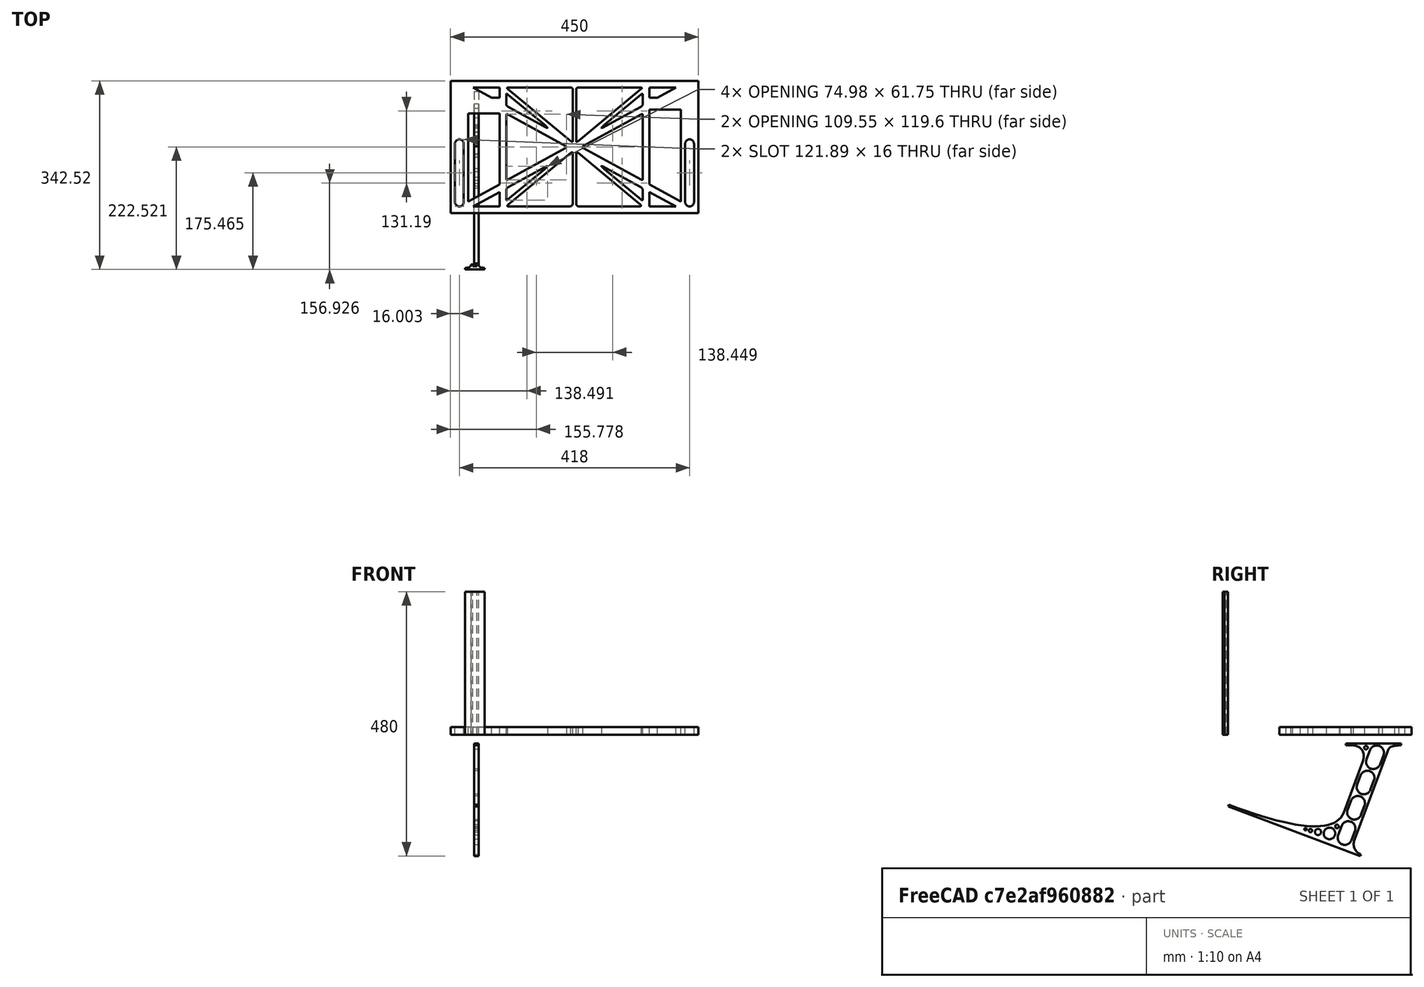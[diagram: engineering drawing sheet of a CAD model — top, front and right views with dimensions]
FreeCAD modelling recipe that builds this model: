
FCSTD DOCUMENT  (FreeCAD 0.19R0.19.2)
Label: laptopStand091
License: All rights reserved
LicenseURL: http://en.wikipedia.org/wiki/All_rights_reserved
objects: Sketcher::SketchObject×3, Part::Extrusion×3
note: 6 computed .brp shape members not serialized (recipe doc carries the construction recipe); baked Part::Feature solids carry a one-line shape summary decoded from their .brp

FEATURE [Sketcher::SketchObject] Sketch
  FullyConstrained = true
  sketch-geometry (244):
    g0: LineSegment StartX=-10.9272 StartY=-82.7794 StartZ=0 EndX=46.0728 EndY=-51.4823 EndZ=0
    g1: LineSegment StartX=366.073 StartY=-91.7794 StartZ=0 EndX=318.073 EndY=-65.424 EndZ=0
    g2: LineSegment StartX=-10.9272 StartY=77.3346 StartZ=0 EndX=-10.9272 EndY=-82.7794 EndZ=0
    g3: LineSegment StartX=375.073 StartY=-82.7794 StartZ=0 EndX=375.073 EndY=83.9235 EndZ=0
    g4: LineSegment StartX=-1.92719 StartY=-91.7794 StartZ=0 EndX=46.0728 EndY=-91.7794 EndZ=0
    g5: LineSegment StartX=318.073 StartY=124.221 StartZ=0 EndX=366.073 EndY=124.221 EndZ=0
    g6: LineSegment StartX=318.073 StartY=83.9235 StartZ=0 EndX=318.073 EndY=-51.4823 EndZ=0
    g7: LineSegment StartX=318.073 StartY=-51.4823 StartZ=0 EndX=375.073 EndY=-82.7794 EndZ=0
    g8: LineSegment StartX=318.073 StartY=-65.424 StartZ=0 EndX=318.073 EndY=-91.7794 EndZ=0
    g9: LineSegment StartX=318.073 StartY=-91.7794 StartZ=0 EndX=366.073 EndY=-91.7794 EndZ=0
    g10: LineSegment StartX=46.0728 StartY=-65.424 StartZ=0 EndX=-1.92719 EndY=-91.7794 EndZ=0
    g11: LineSegment StartX=46.0728 StartY=-65.424 StartZ=0 EndX=46.0728 EndY=-91.7794 EndZ=0
    g12: LineSegment StartX=46.0728 StartY=77.3346 StartZ=0 EndX=46.0728 EndY=-51.4823 EndZ=0
    g13: LineSegment StartX=-42.9272 StartY=136.221 StartZ=0 EndX=-42.9272 EndY=-103.779 EndZ=0
    g14: LineSegment StartX=407.073 StartY=136.221 StartZ=0 EndX=407.073 EndY=-103.779 EndZ=0
    g15: ArcOfCircle CenterX=-26.9272 CenterY=22.1087 CenterZ=0 NormalX=0 NormalY=0 NormalZ=1 AngleXU=0 Radius=8 StartAngle=1e-16 EndAngle=3.14159
    g16: ArcOfCircle CenterX=-26.9272 CenterY=-83.7794 CenterZ=0 NormalX=0 NormalY=0 NormalZ=1 AngleXU=0 Radius=8 StartAngle=3.14159 EndAngle=6.28319
    g17: LineSegment StartX=-34.9272 StartY=22.1087 StartZ=0 EndX=-34.9272 EndY=-83.7794 EndZ=0
    g18: LineSegment StartX=-18.9272 StartY=22.1087 StartZ=0 EndX=-18.9272 EndY=-83.7794 EndZ=0
    g19: ArcOfCircle CenterX=391.073 CenterY=22.1087 CenterZ=0 NormalX=0 NormalY=0 NormalZ=1 AngleXU=0 Radius=8 StartAngle=-4.4e-15 EndAngle=3.14159
    g20: LineSegment StartX=399.073 StartY=22.1087 StartZ=0 EndX=399.073 EndY=-83.7794 EndZ=0
    g21: LineSegment StartX=383.073 StartY=22.1087 StartZ=0 EndX=383.073 EndY=-83.7794 EndZ=0
    g22: ArcOfCircle CenterX=391.073 CenterY=-83.7794 CenterZ=0 NormalX=0 NormalY=0 NormalZ=1 AngleXU=0 Radius=8 StartAngle=3.14159 EndAngle=6.28319
    g23: Circle CenterX=175.022 CenterY=27.0628 CenterZ=0 NormalX=0 NormalY=0 NormalZ=1 AngleXU=0 Radius=1
    g24: Circle CenterX=179.022 CenterY=24.8665 CenterZ=0 NormalX=0 NormalY=0 NormalZ=1 AngleXU=0 Radius=1
    g25: Circle CenterX=179.022 CenterY=27.0628 CenterZ=0 NormalX=0 NormalY=0 NormalZ=1 AngleXU=0 Radius=1
    g26: BSplineCurve PolesCount=3 KnotsCount=2 Degree=2 IsPeriodic=0
    g27: GeomPoint X=175.022 Y=27.0628 Z=0
    g28: GeomPoint X=179.022 Y=27.0628 Z=0
    g29: Circle CenterX=189.124 CenterY=27.0628 CenterZ=0 NormalX=0 NormalY=0 NormalZ=1 AngleXU=0 Radius=1
    g30: Circle CenterX=185.124 CenterY=24.8665 CenterZ=0 NormalX=0 NormalY=0 NormalZ=1 AngleXU=0 Radius=1
    g31: Circle CenterX=185.124 CenterY=27.0628 CenterZ=0 NormalX=0 NormalY=0 NormalZ=1 AngleXU=0 Radius=1
    g32: BSplineCurve PolesCount=3 KnotsCount=2 Degree=2 IsPeriodic=0
    g33: GeomPoint X=189.124 Y=27.0628 Z=0
    g34: GeomPoint X=185.124 Y=27.0628 Z=0
    g35: Circle CenterX=175.022 CenterY=5.37834 CenterZ=0 NormalX=0 NormalY=0 NormalZ=1 AngleXU=0 Radius=1
    g36: Circle CenterX=179.022 CenterY=7.57463 CenterZ=0 NormalX=0 NormalY=0 NormalZ=1 AngleXU=0 Radius=1
    g37: Circle CenterX=179.022 CenterY=5.34704 CenterZ=0 NormalX=0 NormalY=0 NormalZ=1 AngleXU=0 Radius=1
    g38: BSplineCurve PolesCount=3 KnotsCount=2 Degree=2 IsPeriodic=0
    g39: GeomPoint X=175.022 Y=5.37834 Z=0
    g40: GeomPoint X=179.022 Y=5.34704 Z=0
    g41: Circle CenterX=189.124 CenterY=5.37834 CenterZ=0 NormalX=0 NormalY=0 NormalZ=1 AngleXU=0 Radius=1
    g42: Circle CenterX=185.124 CenterY=7.57463 CenterZ=0 NormalX=0 NormalY=0 NormalZ=1 AngleXU=0 Radius=1
    g43: Circle CenterX=185.124 CenterY=5.34704 CenterZ=0 NormalX=0 NormalY=0 NormalZ=1 AngleXU=0 Radius=1
    g44: BSplineCurve PolesCount=3 KnotsCount=2 Degree=2 IsPeriodic=0
    g45: GeomPoint X=189.124 Y=5.37834 Z=0
    g46: GeomPoint X=185.124 Y=5.34704 Z=0
    g47: Circle CenterX=165.871 CenterY=18.1458 CenterZ=0 NormalX=0 NormalY=0 NormalZ=1 AngleXU=0 Radius=1
    g48: Circle CenterX=169.377 CenterY=16.2206 CenterZ=0 NormalX=0 NormalY=0 NormalZ=1 AngleXU=0 Radius=1
    g49: Circle CenterX=165.871 CenterY=14.2954 CenterZ=0 NormalX=0 NormalY=0 NormalZ=1 AngleXU=0 Radius=1
    g50: BSplineCurve PolesCount=3 KnotsCount=2 Degree=2 IsPeriodic=0
    g51: GeomPoint X=165.871 Y=18.1458 Z=0
    g52: GeomPoint X=165.871 Y=14.2954 Z=0
    g53: Circle CenterX=198.275 CenterY=18.1458 CenterZ=0 NormalX=0 NormalY=0 NormalZ=1 AngleXU=0 Radius=1
    g54: Circle CenterX=194.768 CenterY=16.2206 CenterZ=0 NormalX=0 NormalY=0 NormalZ=1 AngleXU=0 Radius=1
    g55: Circle CenterX=198.275 CenterY=14.2954 CenterZ=0 NormalX=0 NormalY=0 NormalZ=1 AngleXU=0 Radius=1
    g56: BSplineCurve PolesCount=3 KnotsCount=2 Degree=2 IsPeriodic=0
    g57: GeomPoint X=198.275 Y=18.1458 Z=0
    g58: GeomPoint X=198.275 Y=14.2954 Z=0
    g59: LineSegment StartX=407.073 StartY=-103.779 StartZ=0 EndX=-42.9272 EndY=-103.779 EndZ=0
    g60: LineSegment StartX=407.073 StartY=136.221 StartZ=0 EndX=-42.9272 EndY=136.221 EndZ=0
    g61: LineSegment StartX=46.0728 StartY=77.3346 StartZ=0 EndX=-10.9272 EndY=77.3346 EndZ=0
    g62: LineSegment StartX=46.0728 StartY=105.865 StartZ=0 EndX=31.5028 EndY=105.865 EndZ=0
    g63: LineSegment StartX=46.0728 StartY=124.221 StartZ=0 EndX=46.0728 EndY=105.865 EndZ=0
    g64: LineSegment StartX=-1.92719 StartY=124.221 StartZ=0 EndX=31.5028 EndY=105.865 EndZ=0
    g65: LineSegment StartX=46.0728 StartY=124.221 StartZ=0 EndX=-1.92719 EndY=124.221 EndZ=0
    g66: LineSegment StartX=318.073 StartY=83.9235 StartZ=0 EndX=375.073 EndY=83.9235 EndZ=0
    g67: LineSegment StartX=318.073 StartY=105.865 StartZ=0 EndX=332.643 EndY=105.865 EndZ=0
    g68: LineSegment StartX=332.643 StartY=105.865 StartZ=0 EndX=366.073 EndY=124.221 EndZ=0
    g69: LineSegment StartX=318.073 StartY=124.221 StartZ=0 EndX=318.073 EndY=105.865 EndZ=0
    g70: Circle CenterX=125.607 CenterY=54.1951 CenterZ=0 NormalX=0 NormalY=0 NormalZ=1 AngleXU=0 Radius=1
    g71: Circle CenterX=139.632 CenterY=46.4944 CenterZ=0 NormalX=0 NormalY=0 NormalZ=1 AngleXU=0 Radius=1
    g72: Circle CenterX=127.326 CenterY=56.7187 CenterZ=0 NormalX=0 NormalY=0 NormalZ=1 AngleXU=0 Radius=1
    g73: BSplineCurve PolesCount=3 KnotsCount=2 Degree=2 IsPeriodic=0
    g74: GeomPoint X=125.607 Y=54.1951 Z=0
    g75: GeomPoint X=127.326 Y=56.7187 Z=0
    g76: Circle CenterX=236.821 CenterY=56.7187 CenterZ=0 NormalX=0 NormalY=0 NormalZ=1 AngleXU=0 Radius=1
    g77: Circle CenterX=224.513 CenterY=46.4944 CenterZ=0 NormalX=0 NormalY=0 NormalZ=1 AngleXU=0 Radius=1
    g78: Circle CenterX=238.538 CenterY=54.1951 CenterZ=0 NormalX=0 NormalY=0 NormalZ=1 AngleXU=0 Radius=1
    g79: BSplineCurve PolesCount=3 KnotsCount=2 Degree=2 IsPeriodic=0
    g80: GeomPoint X=236.821 Y=56.7187 Z=0
    g81: GeomPoint X=238.538 Y=54.1951 Z=0
    g82: Circle CenterX=238.538 CenterY=-21.7539 CenterZ=0 NormalX=0 NormalY=0 NormalZ=1 AngleXU=0 Radius=1
    g83: Circle CenterX=224.513 CenterY=-14.0532 CenterZ=0 NormalX=0 NormalY=0 NormalZ=1 AngleXU=0 Radius=1
    g84: Circle CenterX=236.821 CenterY=-24.2775 CenterZ=0 NormalX=0 NormalY=0 NormalZ=1 AngleXU=0 Radius=1
    g85: BSplineCurve PolesCount=3 KnotsCount=2 Degree=2 IsPeriodic=0
    g86: GeomPoint X=238.538 Y=-21.7539 Z=0
    g87: GeomPoint X=236.821 Y=-24.2775 Z=0
    g88: Circle CenterX=125.607 CenterY=-21.7539 CenterZ=0 NormalX=0 NormalY=0 NormalZ=1 AngleXU=0 Radius=1
    g89: Circle CenterX=139.632 CenterY=-14.0532 CenterZ=0 NormalX=0 NormalY=0 NormalZ=1 AngleXU=0 Radius=1
    g90: Circle CenterX=127.325 CenterY=-24.2775 CenterZ=0 NormalX=0 NormalY=0 NormalZ=1 AngleXU=0 Radius=1
    g91: BSplineCurve PolesCount=3 KnotsCount=2 Degree=2 IsPeriodic=0
    g92: GeomPoint X=125.607 Y=-21.7539 Z=0
    g93: GeomPoint X=127.325 Y=-24.2775 Z=0
    g94: Circle CenterX=302.996 CenterY=111.695 CenterZ=0 NormalX=0 NormalY=0 NormalZ=1 AngleXU=0 Radius=1
    g95: Circle CenterX=306.073 CenterY=114.251 CenterZ=0 NormalX=0 NormalY=0 NormalZ=1 AngleXU=0 Radius=1
    g96: Circle CenterX=306.073 CenterY=110.251 CenterZ=0 NormalX=0 NormalY=0 NormalZ=1 AngleXU=0 Radius=1
    g97: BSplineCurve PolesCount=3 KnotsCount=2 Degree=2 IsPeriodic=0
    g98: GeomPoint X=302.996 Y=111.695 Z=0
    g99: GeomPoint X=306.073 Y=110.251 Z=0
    g100: Circle CenterX=306.073 CenterY=95.2763 CenterZ=0 NormalX=0 NormalY=0 NormalZ=1 AngleXU=0 Radius=1
    g101: Circle CenterX=306.073 CenterY=91.2763 CenterZ=0 NormalX=0 NormalY=0 NormalZ=1 AngleXU=0 Radius=1
    g102: Circle CenterX=302.567 CenterY=89.3511 CenterZ=0 NormalX=0 NormalY=0 NormalZ=1 AngleXU=0 Radius=1
    g103: BSplineCurve PolesCount=3 KnotsCount=2 Degree=2 IsPeriodic=0
    g104: GeomPoint X=306.073 Y=95.2763 Z=0
    g105: GeomPoint X=302.567 Y=89.3511 Z=0
    g106: LineSegment StartX=306.073 StartY=110.251 StartZ=0 EndX=306.073 EndY=95.2763 EndZ=0
    g107: LineSegment StartX=302.996 StartY=111.695 StartZ=0 EndX=236.821 EndY=56.7187 EndZ=0
    g108: LineSegment StartX=238.538 StartY=54.1951 StartZ=0 EndX=302.567 EndY=89.3511 EndZ=0
    g109: Circle CenterX=61.1496 CenterY=111.695 CenterZ=0 NormalX=0 NormalY=0 NormalZ=1 AngleXU=0 Radius=1
    g110: Circle CenterX=58.0728 CenterY=114.251 CenterZ=0 NormalX=0 NormalY=0 NormalZ=1 AngleXU=0 Radius=1
    g111: Circle CenterX=58.0728 CenterY=110.251 CenterZ=0 NormalX=0 NormalY=0 NormalZ=1 AngleXU=0 Radius=1
    g112: BSplineCurve PolesCount=3 KnotsCount=2 Degree=2 IsPeriodic=0
    g113: GeomPoint X=61.1496 Y=111.695 Z=0
    g114: GeomPoint X=58.0728 Y=110.251 Z=0
    g115: Circle CenterX=61.5791 CenterY=89.3511 CenterZ=0 NormalX=0 NormalY=0 NormalZ=1 AngleXU=0 Radius=1
    g116: Circle CenterX=58.0728 CenterY=91.2763 CenterZ=0 NormalX=0 NormalY=0 NormalZ=1 AngleXU=0 Radius=1
    g117: Circle CenterX=58.0728 CenterY=95.2763 CenterZ=0 NormalX=0 NormalY=0 NormalZ=1 AngleXU=0 Radius=1
    g118: BSplineCurve PolesCount=3 KnotsCount=2 Degree=2 IsPeriodic=0
    g119: GeomPoint X=61.5791 Y=89.3511 Z=0
    g120: GeomPoint X=58.0728 Y=95.2763 Z=0
    g121: LineSegment StartX=58.0728 StartY=110.251 StartZ=0 EndX=58.0728 EndY=95.2763 EndZ=0
    g122: LineSegment StartX=61.1496 StartY=111.695 StartZ=0 EndX=127.326 EndY=56.7187 EndZ=0
    g123: LineSegment StartX=125.607 StartY=54.1951 StartZ=0 EndX=61.5791 EndY=89.3511 EndZ=0
    g124: Circle CenterX=61.5791 CenterY=-56.9099 CenterZ=0 NormalX=0 NormalY=0 NormalZ=1 AngleXU=0 Radius=1
    g125: Circle CenterX=58.0728 CenterY=-58.8351 CenterZ=0 NormalX=0 NormalY=0 NormalZ=1 AngleXU=0 Radius=1
    g126: Circle CenterX=58.0728 CenterY=-62.8351 CenterZ=0 NormalX=0 NormalY=0 NormalZ=1 AngleXU=0 Radius=1
    g127: BSplineCurve PolesCount=3 KnotsCount=2 Degree=2 IsPeriodic=0
    g128: GeomPoint X=61.5791 Y=-56.9099 Z=0
    g129: GeomPoint X=58.0728 Y=-62.8351 Z=0
    g130: Circle CenterX=58.0728 CenterY=-77.8102 CenterZ=0 NormalX=0 NormalY=0 NormalZ=1 AngleXU=0 Radius=1
    g131: Circle CenterX=58.0728 CenterY=-81.8102 CenterZ=0 NormalX=0 NormalY=0 NormalZ=1 AngleXU=0 Radius=1
    g132: Circle CenterX=61.1496 CenterY=-79.2541 CenterZ=0 NormalX=0 NormalY=0 NormalZ=1 AngleXU=0 Radius=1
    g133: BSplineCurve PolesCount=3 KnotsCount=2 Degree=2 IsPeriodic=0
    g134: GeomPoint X=58.0728 Y=-77.8102 Z=0
    g135: GeomPoint X=61.1496 Y=-79.2541 Z=0
    g136: LineSegment StartX=58.0728 StartY=-62.8351 StartZ=0 EndX=58.0728 EndY=-77.8102 EndZ=0
    g137: LineSegment StartX=61.1496 StartY=-79.2541 StartZ=0 EndX=127.325 EndY=-24.2775 EndZ=0
    g138: LineSegment StartX=125.607 StartY=-21.7539 StartZ=0 EndX=61.5791 EndY=-56.9099 EndZ=0
    g139: Circle CenterX=302.567 CenterY=-56.9099 CenterZ=0 NormalX=0 NormalY=0 NormalZ=1 AngleXU=0 Radius=1
    g140: Circle CenterX=306.073 CenterY=-58.8351 CenterZ=0 NormalX=0 NormalY=0 NormalZ=1 AngleXU=0 Radius=1
    g141: Circle CenterX=306.073 CenterY=-62.8351 CenterZ=0 NormalX=0 NormalY=0 NormalZ=1 AngleXU=0 Radius=1
    g142: BSplineCurve PolesCount=3 KnotsCount=2 Degree=2 IsPeriodic=0
    g143: GeomPoint X=302.567 Y=-56.9099 Z=0
    g144: GeomPoint X=306.073 Y=-62.8351 Z=0
    g145: Circle CenterX=302.996 CenterY=-79.2541 CenterZ=0 NormalX=0 NormalY=0 NormalZ=1 AngleXU=0 Radius=1
    g146: Circle CenterX=306.073 CenterY=-81.8102 CenterZ=0 NormalX=0 NormalY=0 NormalZ=1 AngleXU=0 Radius=1
    g147: Circle CenterX=306.073 CenterY=-77.8102 CenterZ=0 NormalX=0 NormalY=0 NormalZ=1 AngleXU=0 Radius=1
    g148: BSplineCurve PolesCount=3 KnotsCount=2 Degree=2 IsPeriodic=0
    g149: GeomPoint X=302.996 Y=-79.2541 Z=0
    g150: GeomPoint X=306.073 Y=-77.8102 Z=0
    g151: LineSegment StartX=306.073 StartY=-62.8351 StartZ=0 EndX=306.073 EndY=-77.8102 EndZ=0
    g152: LineSegment StartX=302.996 StartY=-79.2541 StartZ=0 EndX=236.821 EndY=-24.2775 EndZ=0
    g153: LineSegment StartX=238.538 StartY=-21.7539 StartZ=0 EndX=302.567 EndY=-56.9099 EndZ=0
    g154: Circle CenterX=61.6457 CenterY=-88.8112 CenterZ=0 NormalX=0 NormalY=0 NormalZ=1 AngleXU=0 Radius=1
    g155: Circle CenterX=58.0728 CenterY=-91.7794 CenterZ=0 NormalX=0 NormalY=0 NormalZ=1 AngleXU=0 Radius=1
    g156: Circle CenterX=63.9135 CenterY=-91.7794 CenterZ=0 NormalX=0 NormalY=0 NormalZ=1 AngleXU=0 Radius=1
    g157: BSplineCurve PolesCount=3 KnotsCount=2 Degree=2 IsPeriodic=0
    g158: GeomPoint X=61.6457 Y=-88.8112 Z=0
    g159: GeomPoint X=63.9135 Y=-91.7794 Z=0
    g160: Circle CenterX=179.022 CenterY=-85.8163 CenterZ=0 NormalX=0 NormalY=0 NormalZ=1 AngleXU=0 Radius=1
    g161: Circle CenterX=179.022 CenterY=-91.7794 CenterZ=0 NormalX=0 NormalY=0 NormalZ=1 AngleXU=0 Radius=1
    g162: Circle CenterX=171.895 CenterY=-91.7794 CenterZ=0 NormalX=0 NormalY=0 NormalZ=1 AngleXU=0 Radius=1
    g163: BSplineCurve PolesCount=3 KnotsCount=2 Degree=2 IsPeriodic=0
    g164: GeomPoint X=179.022 Y=-85.8163 Z=0
    g165: GeomPoint X=171.895 Y=-91.7794 Z=0
    g166: Circle CenterX=185.124 CenterY=-86.2028 CenterZ=0 NormalX=0 NormalY=0 NormalZ=1 AngleXU=0 Radius=1
    g167: Circle CenterX=185.124 CenterY=-91.7794 CenterZ=0 NormalX=0 NormalY=0 NormalZ=1 AngleXU=0 Radius=1
    g168: Circle CenterX=191.747 CenterY=-91.7794 CenterZ=0 NormalX=0 NormalY=0 NormalZ=1 AngleXU=0 Radius=1
    g169: BSplineCurve PolesCount=3 KnotsCount=2 Degree=2 IsPeriodic=0
    g170: GeomPoint X=185.124 Y=-86.2028 Z=0
    g171: GeomPoint X=191.747 Y=-91.7794 Z=0
    g172: Circle CenterX=299.888 CenterY=-86.6413 CenterZ=0 NormalX=0 NormalY=0 NormalZ=1 AngleXU=0 Radius=1
    g173: Circle CenterX=306.073 CenterY=-91.7794 CenterZ=0 NormalX=0 NormalY=0 NormalZ=1 AngleXU=0 Radius=1
    g174: Circle CenterX=298.776 CenterY=-91.7794 CenterZ=0 NormalX=0 NormalY=0 NormalZ=1 AngleXU=0 Radius=1
    g175: BSplineCurve PolesCount=3 KnotsCount=2 Degree=2 IsPeriodic=0
    g176: GeomPoint X=299.888 Y=-86.6413 Z=0
    g177: GeomPoint X=298.776 Y=-91.7794 Z=0
    g178: LineSegment StartX=189.124 StartY=5.37834 StartZ=0 EndX=299.888 EndY=-86.6413 EndZ=0
    g179: LineSegment StartX=298.776 StartY=-91.7794 StartZ=0 EndX=191.747 EndY=-91.7794 EndZ=0
    g180: LineSegment StartX=185.124 StartY=-86.2028 StartZ=0 EndX=185.124 EndY=5.34704 EndZ=0
    g181: LineSegment StartX=179.022 StartY=5.34704 StartZ=0 EndX=179.022 EndY=-85.8163 EndZ=0
    g182: LineSegment StartX=171.895 StartY=-91.7794 StartZ=0 EndX=63.9135 EndY=-91.7794 EndZ=0
    g183: LineSegment StartX=61.6457 StartY=-88.8112 StartZ=0 EndX=175.022 EndY=5.37834 EndZ=0
    g184: Circle CenterX=302.073 CenterY=124.221 CenterZ=0 NormalX=0 NormalY=0 NormalZ=1 AngleXU=0 Radius=1
    g185: Circle CenterX=306.073 CenterY=124.221 CenterZ=0 NormalX=0 NormalY=0 NormalZ=1 AngleXU=0 Radius=1
    g186: Circle CenterX=302.996 CenterY=121.665 CenterZ=0 NormalX=0 NormalY=0 NormalZ=1 AngleXU=0 Radius=1
    g187: BSplineCurve PolesCount=3 KnotsCount=2 Degree=2 IsPeriodic=0
    g188: GeomPoint X=302.073 Y=124.221 Z=0
    g189: GeomPoint X=302.996 Y=121.665 Z=0
    g190: Circle CenterX=189.124 CenterY=124.221 CenterZ=0 NormalX=0 NormalY=0 NormalZ=1 AngleXU=0 Radius=1
    g191: Circle CenterX=185.124 CenterY=124.221 CenterZ=0 NormalX=0 NormalY=0 NormalZ=1 AngleXU=0 Radius=1
    g192: Circle CenterX=185.124 CenterY=120.221 CenterZ=0 NormalX=0 NormalY=0 NormalZ=1 AngleXU=0 Radius=1
    g193: BSplineCurve PolesCount=3 KnotsCount=2 Degree=2 IsPeriodic=0
    g194: GeomPoint X=189.124 Y=124.221 Z=0
    g195: GeomPoint X=185.124 Y=120.221 Z=0
    g196: Circle CenterX=175.022 CenterY=124.221 CenterZ=0 NormalX=0 NormalY=0 NormalZ=1 AngleXU=0 Radius=1
    g197: Circle CenterX=179.022 CenterY=124.221 CenterZ=0 NormalX=0 NormalY=0 NormalZ=1 AngleXU=0 Radius=1
    g198: Circle CenterX=179.022 CenterY=120.221 CenterZ=0 NormalX=0 NormalY=0 NormalZ=1 AngleXU=0 Radius=1
    g199: BSplineCurve PolesCount=3 KnotsCount=2 Degree=2 IsPeriodic=0
    g200: GeomPoint X=175.022 Y=124.221 Z=0
    g201: GeomPoint X=179.022 Y=120.221 Z=0
    g202: Circle CenterX=62.0728 CenterY=124.221 CenterZ=0 NormalX=0 NormalY=0 NormalZ=1 AngleXU=0 Radius=1
    g203: Circle CenterX=58.0728 CenterY=124.221 CenterZ=0 NormalX=0 NormalY=0 NormalZ=1 AngleXU=0 Radius=1
    g204: Circle CenterX=61.1496 CenterY=121.665 CenterZ=0 NormalX=0 NormalY=0 NormalZ=1 AngleXU=0 Radius=1
    g205: BSplineCurve PolesCount=3 KnotsCount=2 Degree=2 IsPeriodic=0
    g206: GeomPoint X=62.0728 Y=124.221 Z=0
    g207: GeomPoint X=61.1496 Y=121.665 Z=0
    g208: LineSegment StartX=62.0728 StartY=124.221 StartZ=0 EndX=175.022 EndY=124.221 EndZ=0
    g209: LineSegment StartX=179.022 StartY=120.221 StartZ=0 EndX=179.022 EndY=27.0628 EndZ=0
    g210: LineSegment StartX=185.124 StartY=27.0628 StartZ=0 EndX=185.124 EndY=120.221 EndZ=0
    g211: LineSegment StartX=189.124 StartY=124.221 StartZ=0 EndX=302.073 EndY=124.221 EndZ=0
    g212: LineSegment StartX=302.996 StartY=121.665 StartZ=0 EndX=189.124 EndY=27.0628 EndZ=0
    g213: LineSegment StartX=175.022 StartY=27.0628 StartZ=0 EndX=61.1496 EndY=121.665 EndZ=0
    g214: Circle CenterX=61.5791 CenterY=75.4095 CenterZ=0 NormalX=0 NormalY=0 NormalZ=1 AngleXU=0 Radius=1
    g215: Circle CenterX=58.0728 CenterY=77.3346 CenterZ=0 NormalX=0 NormalY=0 NormalZ=1 AngleXU=0 Radius=1
    g216: Circle CenterX=58.0728 CenterY=73.3346 CenterZ=0 NormalX=0 NormalY=0 NormalZ=1 AngleXU=0 Radius=1
    g217: BSplineCurve PolesCount=3 KnotsCount=2 Degree=2 IsPeriodic=0
    g218: GeomPoint X=61.5791 Y=75.4095 Z=0
    g219: GeomPoint X=58.0728 Y=73.3346 Z=0
    g220: Circle CenterX=58.0728 CenterY=-40.8935 CenterZ=0 NormalX=0 NormalY=0 NormalZ=1 AngleXU=0 Radius=1
    g221: Circle CenterX=58.0728 CenterY=-44.8935 CenterZ=0 NormalX=0 NormalY=0 NormalZ=1 AngleXU=0 Radius=1
    g222: Circle CenterX=61.5791 CenterY=-42.9683 CenterZ=0 NormalX=0 NormalY=0 NormalZ=1 AngleXU=0 Radius=1
    g223: BSplineCurve PolesCount=3 KnotsCount=2 Degree=2 IsPeriodic=0
    g224: GeomPoint X=58.0728 Y=-40.8935 Z=0
    g225: GeomPoint X=61.5791 Y=-42.9683 Z=0
    g226: LineSegment StartX=61.5791 StartY=-42.9683 StartZ=0 EndX=165.871 EndY=14.2954 EndZ=0
    g227: LineSegment StartX=165.871 StartY=18.1458 StartZ=0 EndX=61.5791 EndY=75.4095 EndZ=0
    g228: LineSegment StartX=58.0728 StartY=73.3346 StartZ=0 EndX=58.0728 EndY=-40.8935 EndZ=0
    g229: Circle CenterX=302.567 CenterY=-42.9683 CenterZ=0 NormalX=0 NormalY=0 NormalZ=1 AngleXU=0 Radius=1
    g230: Circle CenterX=306.073 CenterY=-44.8935 CenterZ=0 NormalX=0 NormalY=0 NormalZ=1 AngleXU=0 Radius=1
    g231: Circle CenterX=306.073 CenterY=-40.8935 CenterZ=0 NormalX=0 NormalY=0 NormalZ=1 AngleXU=0 Radius=1
    g232: BSplineCurve PolesCount=3 KnotsCount=2 Degree=2 IsPeriodic=0
    g233: GeomPoint X=302.567 Y=-42.9683 Z=0
    g234: GeomPoint X=306.073 Y=-40.8935 Z=0
    g235: Circle CenterX=306.073 CenterY=73.3346 CenterZ=0 NormalX=0 NormalY=0 NormalZ=1 AngleXU=0 Radius=1
    g236: Circle CenterX=306.073 CenterY=77.3346 CenterZ=0 NormalX=0 NormalY=0 NormalZ=1 AngleXU=0 Radius=1
    g237: Circle CenterX=302.567 CenterY=75.4095 CenterZ=0 NormalX=0 NormalY=0 NormalZ=1 AngleXU=0 Radius=1
    g238: BSplineCurve PolesCount=3 KnotsCount=2 Degree=2 IsPeriodic=0
    g239: GeomPoint X=306.073 Y=73.3346 Z=0
    g240: GeomPoint X=302.567 Y=75.4095 Z=0
    g241: LineSegment StartX=302.567 StartY=-42.9683 StartZ=0 EndX=198.275 EndY=14.2954 EndZ=0
    g242: LineSegment StartX=198.275 StartY=18.1458 StartZ=0 EndX=302.567 EndY=75.4095 EndZ=0
    g243: LineSegment StartX=306.073 StartY=73.3346 StartZ=0 EndX=306.073 EndY=-40.8935 EndZ=0
  constraints (415):
    c: Horizontal(g4)
    c: Horizontal(g5)
    c: Coincident(g6,g7)
    c: Coincident(g8,g1)
    c: Tangent(g6,g8)
    c: Coincident(g11,g10)
    c: Coincident(g0,g12)
    c: Block(g7)
    c: Block(g3)
    c: Block(g1)
    c: Block(g8)
    c: Block(g11)
    c: Block(g10)
    c: Block(g0)
    c: Block(g2)
    c: Block(g5)
    c: Block(g9)
    c: Block(g4)
    c: Vertical(g13)
    c: Vertical(g14)
    c: Block(g14)
    c: Block(g13)
    c: Tangent(g15,g18) = 1.5708
    c: Tangent(g15,g17) = -1.5708
    c: Tangent(g17,g16) = -1.5708
    c: Tangent(g18,g16) = 1.5708
    c: Vertical(g17)
    c: Equal(g15,g16)
    c: Block(g18)
    c: Block(g17)
    c: Tangent(g19,g20) = 1.5708
    c: Tangent(g20,g22) = 1.5708
    c: Equal(g19,g22)
    c: Coincident(g21,g19)
    c: Coincident(g21,g22)
    c: Block(g20)
    c: Block(g21)
    c: Weight(g23) = 1
    c: Equal(g23,g24)
    c: Equal(g23,g25)
    c: InternalAlignment(g23,g26)
    c: InternalAlignment(g24,g26)
    c: InternalAlignment(g25,g26)
    c: InternalAlignment(g27,g26)
    c: InternalAlignment(g28,g26)
    c: Weight(g29) = 1
    c: Equal(g29,g30)
    c: Equal(g29,g31)
    c: InternalAlignment(g29,g32)
    c: InternalAlignment(g30,g32)
    c: InternalAlignment(g31,g32)
    c: InternalAlignment(g33,g32)
    c: InternalAlignment(g34,g32)
    c: Block(g32)
    c: Block(g26)
    c: Weight(g35) = 1
    c: Equal(g35,g36)
    c: Equal(g35,g37)
    c: InternalAlignment(g35,g38)
    c: InternalAlignment(g36,g38)
    c: InternalAlignment(g37,g38)
    c: InternalAlignment(g39,g38)
    c: InternalAlignment(g40,g38)
    c: Weight(g41) = 1
    c: Equal(g41,g42)
    c: Equal(g41,g43)
    c: InternalAlignment(g41,g44)
    c: InternalAlignment(g42,g44)
    c: InternalAlignment(g43,g44)
    c: InternalAlignment(g45,g44)
    c: InternalAlignment(g46,g44)
    c: Block(g44)
    c: Block(g38)
    c: Weight(g47) = 1
    c: Equal(g47,g48)
    c: Equal(g47,g49)
    c: InternalAlignment(g47,g50)
    c: InternalAlignment(g48,g50)
    c: InternalAlignment(g49,g50)
    c: InternalAlignment(g51,g50)
    c: InternalAlignment(g52,g50)
    c: Weight(g53) = 1
    c: Equal(g53,g54)
    c: Equal(g53,g55)
    c: InternalAlignment(g53,g56)
    c: InternalAlignment(g54,g56)
    c: InternalAlignment(g55,g56)
    c: InternalAlignment(g57,g56)
    c: InternalAlignment(g58,g56)
    c: Block(g50)
    c: Block(g56)
    c: Coincident(g59,g14)
    c: Coincident(g59,g13)
    c: Horizontal(g59)
    c: Distance(g59) = 450
    c: Coincident(g60,g14)
    c: Coincident(g60,g13)
    c: Horizontal(g60)
    c: Horizontal(g61)
    c: Coincident(g12,g61)
    c: Horizontal(g62)
    c: Vertical(g63)
    c: Block(g63)
    c: Block(g62)
    c: Block(g61)
    c: Distance(g63) = 18.3554
    c: Coincident(g65,g63)
    c: Coincident(g65,g64)
    c: Horizontal(g65)
    c: Block(g65)
    c: Block(g64)
    c: Coincident(g62,g64)
    c: Coincident(g2,g61)
    c: Coincident(g66,g6)
    c: Horizontal(g66)
    c: Horizontal(g67)
    c: Block(g66)
    c: Coincident(g68,g5)
    c: Coincident(g69,g5)
    c: Coincident(g69,g67)
    c: Vertical(g69)
    c: Block(g69)
    c: Coincident(g67,g68)
    c: Block(g68)
    c: Coincident(g3,g66)
    c: Weight(g70) = 1
    c: Equal(g70,g71)
    c: Equal(g70,g72)
    c: InternalAlignment(g70,g73)
    c: InternalAlignment(g71,g73)
    c: InternalAlignment(g72,g73)
    c: InternalAlignment(g74,g73)
    c: InternalAlignment(g75,g73)
    c: Block(g73)
    c: Weight(g76) = 1
    c: Equal(g76,g77)
    c: Equal(g76,g78)
    c: InternalAlignment(g76,g79)
    c: InternalAlignment(g77,g79)
    c: InternalAlignment(g78,g79)
    c: InternalAlignment(g80,g79)
    c: InternalAlignment(g81,g79)
    c: Block(g79)
    c: Weight(g82) = 1
    c: Equal(g82,g83)
    c: Equal(g82,g84)
    c: InternalAlignment(g82,g85)
    c: InternalAlignment(g83,g85)
    c: InternalAlignment(g84,g85)
    c: InternalAlignment(g86,g85)
    c: InternalAlignment(g87,g85)
    c: Block(g85)
    c: Weight(g88) = 1
    c: Equal(g88,g89)
    c: Equal(g88,g90)
    c: InternalAlignment(g88,g91)
    c: InternalAlignment(g89,g91)
    c: InternalAlignment(g90,g91)
    c: InternalAlignment(g92,g91)
    c: InternalAlignment(g93,g91)
    c: Block(g91)
    c: Weight(g94) = 1
    c: Equal(g94,g95)
    c: Equal(g94,g96)
    c: InternalAlignment(g94,g97)
    c: InternalAlignment(g95,g97)
    c: InternalAlignment(g96,g97)
    c: InternalAlignment(g98,g97)
    c: InternalAlignment(g99,g97)
    c: Weight(g100) = 1
    c: Equal(g100,g101)
    c: Equal(g100,g102)
    c: InternalAlignment(g100,g103)
    c: InternalAlignment(g101,g103)
    c: InternalAlignment(g102,g103)
    c: InternalAlignment(g104,g103)
    c: InternalAlignment(g105,g103)
    c: Block(g97)
    c: Block(g103)
    c: Coincident(g106,g97)
    c: Coincident(g106,g103)
    c: Vertical(g106)
    c: Coincident(g107,g97)
    c: Coincident(g107,g79)
    c: Coincident(g108,g79)
    c: Coincident(g108,g103)
    c: Weight(g109) = 1
    c: Equal(g109,g110)
    c: Equal(g109,g111)
    c: InternalAlignment(g109,g112)
    c: InternalAlignment(g110,g112)
    c: InternalAlignment(g111,g112)
    c: InternalAlignment(g113,g112)
    c: InternalAlignment(g114,g112)
    c: Weight(g115) = 1
    c: Equal(g115,g116)
    c: Equal(g115,g117)
    c: InternalAlignment(g115,g118)
    c: InternalAlignment(g116,g118)
    c: InternalAlignment(g117,g118)
    c: InternalAlignment(g119,g118)
    c: InternalAlignment(g120,g118)
    c: Block(g112)
    c: Block(g118)
    c: Coincident(g121,g112)
    c: Coincident(g121,g118)
    c: Vertical(g121)
    c: Coincident(g122,g112)
    c: Coincident(g122,g73)
    c: Coincident(g123,g73)
    c: Coincident(g123,g118)
    c: Weight(g124) = 1
    c: Equal(g124,g125)
    c: Equal(g124,g126)
    c: InternalAlignment(g124,g127)
    c: InternalAlignment(g125,g127)
    c: InternalAlignment(g126,g127)
    c: InternalAlignment(g128,g127)
    c: InternalAlignment(g129,g127)
    c: Weight(g130) = 1
    c: Equal(g130,g131)
    c: Equal(g130,g132)
    c: InternalAlignment(g130,g133)
    c: InternalAlignment(g131,g133)
    c: InternalAlignment(g132,g133)
    c: InternalAlignment(g134,g133)
    c: InternalAlignment(g135,g133)
    c: Block(g127)
    c: Block(g133)
    c: Coincident(g136,g127)
    c: Coincident(g136,g133)
    c: Vertical(g136)
    c: Coincident(g137,g133)
    c: Coincident(g137,g91)
    c: Coincident(g138,g91)
    c: Coincident(g138,g127)
    c: Weight(g139) = 1
    c: Equal(g139,g140)
    c: Equal(g139,g141)
    c: InternalAlignment(g139,g142)
    c: InternalAlignment(g140,g142)
    c: InternalAlignment(g141,g142)
    c: InternalAlignment(g143,g142)
    c: InternalAlignment(g144,g142)
    c: Weight(g145) = 1
    c: Equal(g145,g146)
    c: Equal(g145,g147)
    c: InternalAlignment(g145,g148)
    c: InternalAlignment(g146,g148)
    c: InternalAlignment(g147,g148)
    c: InternalAlignment(g149,g148)
    c: InternalAlignment(g150,g148)
    c: Block(g142)
    c: Block(g148)
    c: Coincident(g151,g142)
    c: Coincident(g151,g148)
    c: Vertical(g151)
    c: Coincident(g152,g148)
    c: Coincident(g152,g85)
    c: Coincident(g153,g85)
    c: Coincident(g153,g142)
    c: Weight(g154) = 1
    c: Equal(g154,g155)
    c: Equal(g154,g156)
    c: InternalAlignment(g154,g157)
    c: InternalAlignment(g155,g157)
    c: InternalAlignment(g156,g157)
    c: InternalAlignment(g158,g157)
    c: InternalAlignment(g159,g157)
    c: Weight(g160) = 1
    c: Equal(g160,g161)
    c: Equal(g160,g162)
    c: InternalAlignment(g160,g163)
    c: InternalAlignment(g161,g163)
    c: InternalAlignment(g162,g163)
    c: InternalAlignment(g164,g163)
    c: InternalAlignment(g165,g163)
    c: Weight(g166) = 1
    c: Equal(g166,g167)
    c: Equal(g166,g168)
    c: InternalAlignment(g166,g169)
    c: InternalAlignment(g167,g169)
    c: InternalAlignment(g168,g169)
    c: InternalAlignment(g170,g169)
    c: InternalAlignment(g171,g169)
    c: Weight(g172) = 1
    c: Equal(g172,g173)
    c: Equal(g172,g174)
    c: InternalAlignment(g172,g175)
    c: InternalAlignment(g173,g175)
    c: InternalAlignment(g174,g175)
    c: InternalAlignment(g176,g175)
    c: InternalAlignment(g177,g175)
    c: Block(g175)
    c: Block(g169)
    c: Block(g163)
    c: Block(g157)
    c: Coincident(g178,g44)
    c: Coincident(g178,g175)
    c: Coincident(g179,g175)
    c: Coincident(g179,g169)
    c: Horizontal(g179)
    c: Coincident(g180,g169)
    c: Coincident(g180,g44)
    c: Vertical(g180)
    c: Coincident(g181,g38)
    c: Coincident(g181,g163)
    c: Vertical(g181)
    c: Coincident(g182,g163)
    c: Coincident(g182,g157)
    c: Horizontal(g182)
    c: Coincident(g183,g157)
    c: Coincident(g183,g38)
    c: Weight(g184) = 1
    c: Equal(g184,g185)
    c: Equal(g184,g186)
    c: InternalAlignment(g184,g187)
    c: InternalAlignment(g185,g187)
    c: InternalAlignment(g186,g187)
    c: InternalAlignment(g188,g187)
    c: InternalAlignment(g189,g187)
    c: Weight(g190) = 1
    c: Equal(g190,g191)
    c: Equal(g190,g192)
    c: InternalAlignment(g190,g193)
    c: InternalAlignment(g191,g193)
    c: InternalAlignment(g192,g193)
    c: InternalAlignment(g194,g193)
    c: InternalAlignment(g195,g193)
    c: Weight(g196) = 1
    c: Equal(g196,g197)
    c: Equal(g196,g198)
    c: InternalAlignment(g196,g199)
    c: InternalAlignment(g197,g199)
    c: InternalAlignment(g198,g199)
    c: InternalAlignment(g200,g199)
    c: InternalAlignment(g201,g199)
    c: Weight(g202) = 1
    c: Equal(g202,g203)
    c: Equal(g202,g204)
    c: InternalAlignment(g202,g205)
    c: InternalAlignment(g203,g205)
    c: InternalAlignment(g204,g205)
    c: InternalAlignment(g206,g205)
    c: InternalAlignment(g207,g205)
    c: Block(g205)
    c: Block(g199)
    c: Block(g193)
    c: Block(g187)
    c: Coincident(g208,g205)
    c: Coincident(g208,g199)
    c: Horizontal(g208)
    c: Coincident(g209,g199)
    c: Coincident(g209,g26)
    c: Vertical(g209)
    c: Coincident(g210,g32)
    c: Coincident(g210,g193)
    c: Vertical(g210)
    c: Coincident(g211,g193)
    c: Coincident(g211,g187)
    c: Horizontal(g211)
    c: Coincident(g212,g187)
    c: Coincident(g212,g32)
    c: Coincident(g213,g26)
    c: Coincident(g213,g205)
    c: Weight(g214) = 1
    c: Equal(g214,g215)
    c: Equal(g214,g216)
    c: InternalAlignment(g214,g217)
    c: InternalAlignment(g215,g217)
    c: InternalAlignment(g216,g217)
    c: InternalAlignment(g218,g217)
    c: InternalAlignment(g219,g217)
    c: Weight(g220) = 1
    c: Equal(g220,g221)
    c: Equal(g220,g222)
    c: InternalAlignment(g220,g223)
    c: InternalAlignment(g221,g223)
    c: InternalAlignment(g222,g223)
    c: InternalAlignment(g224,g223)
    c: InternalAlignment(g225,g223)
    c: Block(g223)
    c: Block(g217)
    c: Coincident(g226,g223)
    c: Coincident(g226,g50)
    c: Coincident(g227,g50)
    c: Coincident(g227,g217)
    c: Coincident(g228,g217)
    c: Coincident(g228,g223)
    c: Vertical(g228)
    c: Weight(g229) = 1
    c: Equal(g229,g230)
    c: Equal(g229,g231)
    c: InternalAlignment(g229,g232)
    c: InternalAlignment(g230,g232)
    c: InternalAlignment(g231,g232)
    c: InternalAlignment(g233,g232)
    c: InternalAlignment(g234,g232)
    c: Weight(g235) = 1
    c: Equal(g235,g236)
    c: Equal(g235,g237)
    c: InternalAlignment(g235,g238)
    c: InternalAlignment(g236,g238)
    c: InternalAlignment(g237,g238)
    c: InternalAlignment(g239,g238)
    c: InternalAlignment(g240,g238)
    c: Block(g238)
    c: Block(g232)
    c: Coincident(g241,g232)
    c: Coincident(g241,g56)
    c: Coincident(g242,g56)
    c: Coincident(g242,g238)
    c: Coincident(g243,g238)
    c: Coincident(g243,g232)
    c: Vertical(g243)
FEATURE [Sketcher::SketchObject] Sketch001
  FullyConstrained = true
  MapMode = 4
  Placement = pos=(0,0,0) rot=(0.57735,0.57735,0.57735;2.0944rad)
  Support = -> [Sketch]
  sketch-geometry (46):
    g0: BSplineCurve PolesCount=3 KnotsCount=2 Degree=2 IsPeriodic=0
    g1: ArcOfCircle CenterX=73.1223 CenterY=-32.291 CenterZ=0 NormalX=0 NormalY=0 NormalZ=1 AngleXU=0 Radius=13 StartAngle=5.92268 EndAngle=9.06428
    g2: ArcOfCircle CenterX=66.7816 CenterY=-49.1439 CenterZ=0 NormalX=0 NormalY=0 NormalZ=1 AngleXU=0 Radius=13 StartAngle=2.78068 EndAngle=5.92131
    g3: ArcOfCircle CenterX=55.9263 CenterY=-78.1807 CenterZ=0 NormalX=0 NormalY=0 NormalZ=1 AngleXU=0 Radius=13 StartAngle=5.92268 EndAngle=9.06428
    g4: ArcOfCircle CenterX=49.5884 CenterY=-95.0342 CenterZ=0 NormalX=0 NormalY=0 NormalZ=1 AngleXU=0 Radius=13 StartAngle=2.78068 EndAngle=5.92131
    g5: ArcOfCircle CenterX=38.7206 CenterY=-124.067 CenterZ=0 NormalX=0 NormalY=0 NormalZ=1 AngleXU=0 Radius=13 StartAngle=5.92268 EndAngle=9.06428
    g6: ArcOfCircle CenterX=32.3875 CenterY=-140.92 CenterZ=0 NormalX=0 NormalY=0 NormalZ=1 AngleXU=0 Radius=13 StartAngle=2.78068 EndAngle=5.92131
    g7: ArcOfCircle CenterX=21.4715 CenterY=-169.934 CenterZ=0 NormalX=0 NormalY=0 NormalZ=1 AngleXU=0 Radius=13 StartAngle=5.92268 EndAngle=9.06428
    g8: ArcOfCircle CenterX=15.1336 CenterY=-186.787 CenterZ=0 NormalX=0 NormalY=0 NormalZ=1 AngleXU=0 Radius=13 StartAngle=2.78068 EndAngle=5.92131
    g9-g12: Circle x4 (B-spline internal-alignment scaffolding for g13; pole/knot coordinates omitted)
    g13: BSplineCurve PolesCount=4 KnotsCount=2 Degree=3 IsPeriodic=0
    g14: GeomPoint X=28.8094 Y=-19.0875 Z=0
    g15: GeomPoint X=47.0443 Y=-50.4712 Z=0
    g16: Circle CenterX=53.5586 CenterY=-23.2695 CenterZ=0 NormalX=0 NormalY=0 NormalZ=1 AngleXU=0 Radius=3.24518
    g17: Circle CenterX=-195.441 CenterY=-127.082 CenterZ=0 NormalX=0 NormalY=0 NormalZ=1 AngleXU=0 Radius=1
    g18: Circle CenterX=-8.24091 CenterY=-197.481 CenterZ=0 NormalX=0 NormalY=0 NormalZ=1 AngleXU=0 Radius=1
    g19: Circle CenterX=12.8789 CenterY=-141.321 CenterZ=0 NormalX=0 NormalY=0 NormalZ=1 AngleXU=0 Radius=1
    g20: BSplineCurve PolesCount=3 KnotsCount=2 Degree=2 IsPeriodic=0
    g21: GeomPoint X=-195.441 Y=-127.082 Z=0
    g22: GeomPoint X=12.8789 Y=-141.321 Z=0
    g23: Circle CenterX=-12.8016 CenterY=-179.036 CenterZ=0 NormalX=0 NormalY=0 NormalZ=1 AngleXU=0 Radius=10.5072
    g24: Circle CenterX=0.933922 CenterY=-166.43 CenterZ=0 NormalX=0 NormalY=0 NormalZ=1 AngleXU=0 Radius=3.26661
    g25: Circle CenterX=-33.5518 CenterY=-176.44 CenterZ=0 NormalX=0 NormalY=0 NormalZ=1 AngleXU=0 Radius=5.64388
    g26: Circle CenterX=-47.2366 CenterY=-173.859 CenterZ=0 NormalX=0 NormalY=0 NormalZ=1 AngleXU=0 Radius=3.01653
    g27: Circle CenterX=-56.2595 CenterY=-171.456 CenterZ=0 NormalX=0 NormalY=0 NormalZ=1 AngleXU=0 Radius=2.12826
    g28: ArcOfCircle CenterX=51.2151 CenterY=-198.473 CenterZ=0 NormalX=0 NormalY=0 NormalZ=1 AngleXU=0 Radius=20 StartAngle=2.78189 EndAngle=4.35269
    g29: LineSegment StartX=32.4951 StartY=-191.433 StartZ=0 EndX=94.6578 EndY=-26.1352 EndZ=0
    g30: LineSegment StartX=43.1192 StartY=-220.001 StartZ=0 EndX=-196.497 EndY=-129.89 EndZ=0
    g31: LineSegment StartX=43.1192 StartY=-220.001 StartZ=0 EndX=44.1752 EndY=-217.193 EndZ=0
    g32: LineSegment StartX=117.223 StartY=-19.0875 StartZ=0 EndX=117.223 EndY=-16.0875 EndZ=0
    g33: LineSegment StartX=117.223 StartY=-16.0875 StartZ=0 EndX=17.2232 EndY=-16.0875 EndZ=0
    g34: LineSegment StartX=17.2232 StartY=-16.0875 StartZ=0 EndX=17.2232 EndY=-19.0875 EndZ=0
    g35: LineSegment StartX=28.8094 StartY=-19.0875 StartZ=0 EndX=17.2232 EndY=-19.0875 EndZ=0
    g36: LineSegment StartX=47.0443 StartY=-50.4712 StartZ=0 EndX=12.8789 EndY=-141.321 EndZ=0
    g37: LineSegment StartX=-195.441 StartY=-127.082 StartZ=0 EndX=-196.497 EndY=-129.89 EndZ=0
    g38: LineSegment StartX=85.2866 StartY=-36.8766 StartZ=0 EndX=78.9396 EndY=-53.7463 EndZ=0
    g39: LineSegment StartX=60.9579 StartY=-27.7053 StartZ=0 EndX=54.6191 EndY=-44.5532 EndZ=0
    g40: LineSegment StartX=68.0907 StartY=-82.7664 StartZ=0 EndX=61.7465 EndY=-99.6365 EndZ=0
    g41: LineSegment StartX=43.7619 StartY=-73.595 StartZ=0 EndX=37.426 EndY=-90.4435 EndZ=0
    g42: LineSegment StartX=50.885 StartY=-128.652 StartZ=0 EndX=44.5456 EndY=-145.522 EndZ=0
    g43: LineSegment StartX=26.5562 StartY=-119.481 StartZ=0 EndX=20.2251 EndY=-136.329 EndZ=0
    g44: LineSegment StartX=9.3071 StartY=-165.349 StartZ=0 EndX=2.97115 EndY=-182.197 EndZ=0
    g45: LineSegment StartX=33.6358 StartY=-174.52 StartZ=0 EndX=27.2917 EndY=-191.39 EndZ=0
  constraints (71):
    c: Block(g0)
    c: Block(g1)
    c: Block(g2)
    c: Block(g4)
    c: Block(g3)
    c: Block(g6)
    c: Block(g5)
    c: Block(g8)
    c: Block(g7)
    c: Weight(g9) = 1
    c: Equal(g9,g10)
    c: Equal(g9,g11)
    c: Equal(g9,g12)
    c: InternalAlignment(g9-g12 -> g13) x4
    c: InternalAlignment(g14,g13)
    c: InternalAlignment(g15,g13)
    c: Block(g16)
    c: Weight(g17) = 1
    c: Equal(g17,g18)
    c: Equal(g17,g19)
    c: InternalAlignment(g17,g20)
    c: InternalAlignment(g18,g20)
    c: InternalAlignment(g19,g20)
    c: InternalAlignment(g21,g20)
    c: InternalAlignment(g22,g20)
    c: Block(g20)
    c: Block(g23)
    c: Block(g24)
    c: Block(g25)
    c: Block(g26)
    c: Block(g27)
    c: Block(g28)
    c: Coincident(g29,g28)
    c: Coincident(g29,g0)
    c: Block(g13)
    c: Coincident(g31,g30)
    c: Coincident(g31,g28)
    c: Block(g31)
    c: Coincident(g32,g0)
    c: Vertical(g32)
    c: Coincident(g33,g32)
    c: Horizontal(g33)
    c: Coincident(g34,g33)
    c: Vertical(g34)
    c: Block(g33)
    c: Coincident(g35,g13)
    c: Coincident(g35,g34)
    c: Horizontal(g35)
    c: Coincident(g36,g13)
    c: Coincident(g36,g20)
    c: Coincident(g37,g20)
    c: Coincident(g37,g30)
    c: Block(g30)
    c: Coincident(g38,g1)
    c: Coincident(g38,g2)
    c: Coincident(g39,g1)
    c: Coincident(g39,g2)
    c: Coincident(g40,g3)
    c: Coincident(g40,g4)
    c: Coincident(g41,g3)
    c: Coincident(g41,g4)
    c: Coincident(g42,g5)
    c: Coincident(g42,g6)
    c: Coincident(g43,g5)
    c: Coincident(g43,g6)
    c: Coincident(g44,g7)
    c: Coincident(g44,g8)
    c: Coincident(g45,g7)
    c: Coincident(g45,g8)
    c: Distance(g30) = 256
    c: Distance(g33) = 100
FEATURE [Part::Extrusion] Extrude002
  Base = -> Sketch001
  Dir = (1,0,0)
  DirMode = 2
  FaceMakerClass = Part::FaceMakerBullseye
  LengthFwd = 8
  LengthRev = 0
  Solid = true
  Symmetric = false
FEATURE [Sketcher::SketchObject] Sketch002
  FullyConstrained = true
  sketch-geometry (20):
    g0: LineSegment StartX=-2.77179 StartY=-200.304 StartZ=0 EndX=5.22821 EndY=-200.304 EndZ=0
    g1: LineSegment StartX=5.22821 StartY=-200.304 StartZ=0 EndX=5.22821 EndY=-197.304 EndZ=0
    g2: LineSegment StartX=-2.77179 StartY=-200.304 StartZ=0 EndX=-2.77179 EndY=-197.304 EndZ=0
    g3: LineSegment StartX=5.22821 StartY=-197.304 StartZ=0 EndX=8.22821 EndY=-197.304 EndZ=0
    g4: LineSegment StartX=-2.77179 StartY=-197.304 StartZ=0 EndX=-5.77179 EndY=-197.304 EndZ=0
    g5: LineSegment StartX=19.2282 StartY=-203.304 StartZ=0 EndX=19.2282 EndY=-206.304 EndZ=0
    g6: LineSegment StartX=-16.7718 StartY=-203.304 StartZ=0 EndX=-16.7718 EndY=-206.304 EndZ=0
    g7: LineSegment StartX=-16.7718 StartY=-206.304 StartZ=0 EndX=19.2282 EndY=-206.304 EndZ=0
    g8: Circle CenterX=-16.7718 CenterY=-203.304 CenterZ=0 NormalX=0 NormalY=0 NormalZ=1 AngleXU=0 Radius=1
    g9: Circle CenterX=-5.77179 CenterY=-203.304 CenterZ=0 NormalX=0 NormalY=0 NormalZ=1 AngleXU=0 Radius=1
    g10: Circle CenterX=-5.77179 CenterY=-197.304 CenterZ=0 NormalX=0 NormalY=0 NormalZ=1 AngleXU=0 Radius=1
    g11: BSplineCurve PolesCount=3 KnotsCount=2 Degree=2 IsPeriodic=0
    g12: GeomPoint X=-16.7718 Y=-203.304 Z=0
    g13: GeomPoint X=-5.77179 Y=-197.304 Z=0
    g14: Circle CenterX=19.2282 CenterY=-203.304 CenterZ=0 NormalX=0 NormalY=0 NormalZ=1 AngleXU=0 Radius=1
    g15: Circle CenterX=8.22821 CenterY=-203.304 CenterZ=0 NormalX=0 NormalY=0 NormalZ=1 AngleXU=0 Radius=1
    g16: Circle CenterX=8.22821 CenterY=-197.304 CenterZ=0 NormalX=0 NormalY=0 NormalZ=1 AngleXU=0 Radius=1
    g17: BSplineCurve PolesCount=3 KnotsCount=2 Degree=2 IsPeriodic=0
    g18: GeomPoint X=19.2282 Y=-203.304 Z=0
    g19: GeomPoint X=8.22821 Y=-197.304 Z=0
  constraints (41):
    c: Horizontal(g0)
    c: Distance(g0) = 8
    c: Coincident(g1,g0)
    c: Vertical(g1)
    c: Distance(g1) = 3
    c: Coincident(g2,g0)
    c: Vertical(g2)
    c: Distance(g2) = 3
    c: Coincident(g3,g1)
    c: Horizontal(g3)
    c: Distance(g3) = 3
    c: Coincident(g4,g2)
    c: Horizontal(g4)
    c: Distance(g4) = 3
    c: Vertical(g5)
    c: Vertical(g6)
    c: Coincident(g7,g6)
    c: Coincident(g7,g5)
    c: Weight(g8) = 1
    c: Equal(g8,g9)
    c: Equal(g8,g10)
    c: Coincident(g11,g4)
    c: InternalAlignment(g8,g11)
    c: InternalAlignment(g9,g11)
    c: InternalAlignment(g10,g11)
    c: InternalAlignment(g12,g11)
    c: InternalAlignment(g13,g11)
    c: Coincident(g17,g5)
    c: Weight(g14) = 1
    c: Equal(g14,g15)
    c: Equal(g14,g16)
    c: Coincident(g17,g3)
    c: InternalAlignment(g14,g17)
    c: InternalAlignment(g15,g17)
    c: InternalAlignment(g16,g17)
    c: InternalAlignment(g18,g17)
    c: InternalAlignment(g19,g17)
    c: Block(g7)
    c: Block(g17)
    c: Block(g11)
    c: Block(g6)
FEATURE [Part::Extrusion] Extrude003
  Base = -> Sketch002
  Dir = (0,0,1)
  DirMode = 2
  FaceMakerClass = Part::FaceMakerBullseye
  LengthFwd = 260
  LengthRev = 0
  Solid = true
  Symmetric = false
FEATURE [Part::Extrusion] Extrude
  Base = -> Sketch
  Dir = (0,0,1)
  DirMode = 2
  FaceMakerClass = Part::FaceMakerBullseye
  LengthFwd = 14
  LengthRev = 0
  Solid = true
  Symmetric = false
